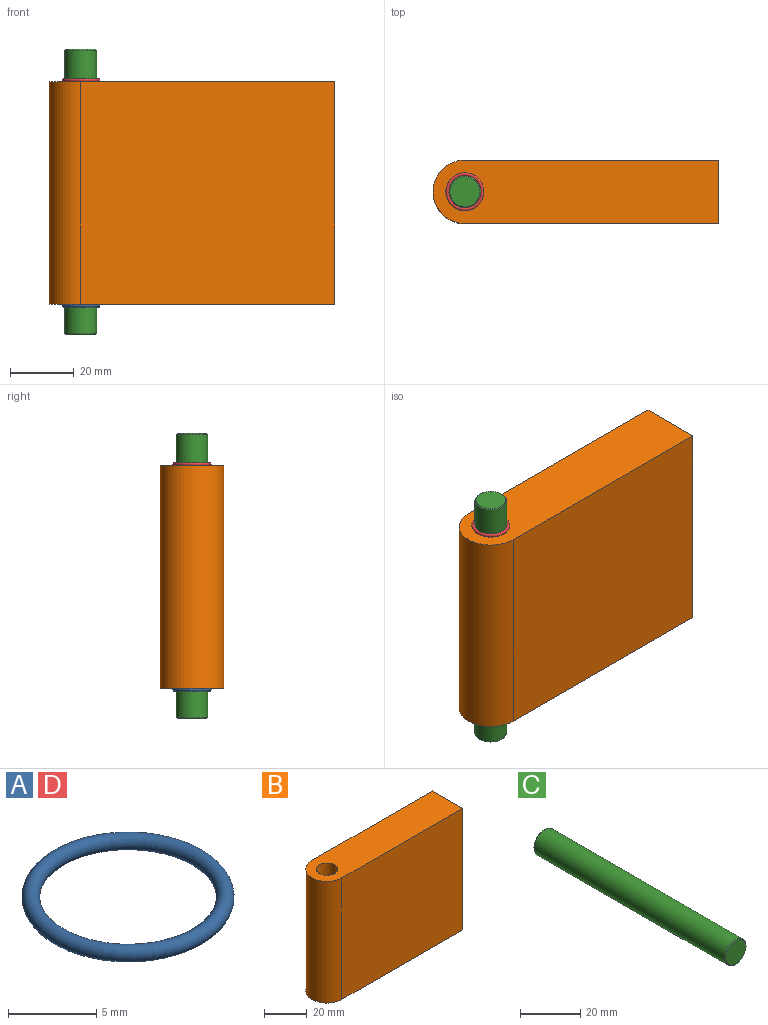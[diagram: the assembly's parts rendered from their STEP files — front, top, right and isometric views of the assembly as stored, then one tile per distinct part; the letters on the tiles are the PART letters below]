
ASSEMBLY  parts=4 mates=3
PART A: 1 faces, bbox 13x13x1 mm
  f0: torus R=5.5mm, axis (0,0,1), area 108.6mm2
PART B: 7 faces, bbox 90x20x70 mm
  f0: plane 90x20mm, normal (0,0,-1), area 1678.5mm2, adj f1,f3,f4,f5,f6
  f1: plane 70x20mm, normal (1,0,0), area 1400mm2, adj f0,f2,f3,f4
  f2: plane 90x20mm, normal (0,0,1), area 1678.5mm2, adj f1,f3,f4,f5,f6
  f3: plane 80x70mm, normal (0,-1,0), area 5600mm2, adj f0,f1,f2,f6
  f4: plane 80x70mm, normal (0,1,0), area 5600mm2, adj f0,f1,f2,f6
  f5: cylinder r=5mm len=70mm, axis (0,0,1), area 2199.1mm2, adj f0,f2
  f6: cylinder r=10mm len=70mm, axis (0,0,1), area 2199.1mm2, adj f0,f2,f3,f4
PART C: 5 faces, bbox 10x90x10 mm
  f0: cylinder r=5mm len=89.4mm, axis (0,1,0), area 2808.6mm2, adj f3,f4
  f1: plane 9.4x9.4mm, normal (0,-1,0), area 69.4mm2, adj f4
  f2: plane 9.4x9.4mm, normal (0,1,0), area 69.4mm2, adj f3
  f3: cone r=5mm half-angle=45deg, axis (0,-1,0), area 12.9mm2, adj f0,f2
  f4: cone r=4.7mm half-angle=45deg, axis (0,1,0), area 12.9mm2, adj f0,f1
PART D: same geometry as A
PLACE A t=(-120.62,14.96,-37.15)mm
PLACE B t=(-44.59,24.96,-12.92)mm
PLACE C rot(axis=(1,0,0),90deg) t=(-34.59,14.96,67.38)mm
PLACE D t=(-120.62,14.96,33.85)mm
MATE planar D.f0 <-> B.f5  axis (0,0,1) through (-34.59,14.96,57.58)mm
MATE planar C.f0 <-> B.f5  axis (0,0,1) through (-34.59,14.96,67.08)mm
MATE planar A.f0 <-> B.f5  axis (0,0,1) through (-34.59,14.96,-13.42)mm
